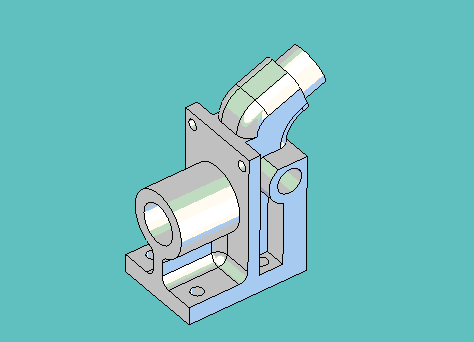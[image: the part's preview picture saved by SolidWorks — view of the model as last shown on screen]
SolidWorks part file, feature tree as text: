
SOLIDWORKS PART (.sldprt)
format: sldprt  version: not decoded by parser v0  size: 1,539,072 bytes
history: native  units: mm
features: sketch x19, boolean_combine x9, extrude x8, cut_extrude x8, fillet x3, material x1, revolve x1, chamfer x1, sweep x1 (+11 scaffold rows collapsed)
feature tree (62):
  scaffold x11  (default folders/planes/origin — collapsed)
  material  "Material <not specified>"
  sketch  "Sketch1"  dims[D1=4.7498mm D2=11.43mm D3=11.43mm D4=31.75mm]
  extrude  "Extrude1"  Depth=38.1mm
  sketch  "Sketch5"  dims[D1=5.7658mm D2=5.7658mm D3=14.1732mm]
  extrude  "Extrude7"  Depth=4.7752mm
  boolean_combine  "Combine4"
  sketch  "Sketch6"  dims[D2=7.366mm D1=20.6502mm]
  extrude  "Extrude8"  Depth=38.1mm
  boolean_combine  "Combine5"
  sketch  "Sketch7"  dims[D1=10.287mm]
  extrude  "Extrude10"  Depth=23.0632mm
  boolean_combine  "Combine6"
  sketch  "Sketch8"  dims[D1=6.604mm D2=4.7752mm]
  extrude  "Extrude11"  Depth=17.4498mm
  boolean_combine  "Combine7"
  sketch  "Sketch9"  dims[c1.D3=6.5278mm c1.D1=28.956mm c1.D2=4.7625mm c2.D1=27.1272mm]
  extrude  "Extrude12"  Depth=38.1mm
  boolean_combine  "Combine8"
  sketch  "Sketch11"  dims[c1.D1=0.381mm c1.D2=3.175mm c2.D1=3.175mm c2.D3=0.254mm c2.D4=7.62mm c2.D2=0.381mm]
  revolve  "Revolve2"  Angle=360deg
  boolean_combine  "Combine11"
  sketch  "Sketch12"  dims[c1.D1=3.175mm c1.D2=3.175mm c1.D3=3.175mm c1.D7=3.175mm c1.D4=9.525mm c1.D5=7.9248mm c1.D6=7.9248mm c2.D7=26.9748mm c2.D8=26.9748mm c2.D4=26.9875mm c2.D3=7.9248mm c2.D6=9.525mm c2.D5=7.9248mm c3.D8=7.9248mm c3.D9=9.525mm c4.D8=7.9248mm]
  extrude  "Extrude14"  Depth=12.7mm
  boolean_combine  "Combine12"
  chamfer  "Chamfer1"  Distance=0.889mm Angle=15deg
  sketch  "Sketch21"  dims[D1=3.175mm D2=15.875mm]
  cut_extrude  "Cut-Extrude6"  [1 undecoded]
  sketch  "Sketch24"  dims[c1.D2=2.032mm c1.D3=~2.38125mm c1.D4=~2.38125mm c1.D5=3.175mm c1.D1=4.7625mm c2.D3=3.175mm c2.D4=1.5875mm c2.D5=1.5875mm c2.D1=0.0mm]
  cut_extrude  "Cut-Extrude9"  [1 undecoded]
  fillet  "Fillet1"  Radius=2.38125mm
  sketch  "Sketch25"  dims[c1.D2=6.5278mm c1.D1=3.175mm c2.D2=22.225mm c2.D3=6.35mm c3.D2=1.778mm c3.D4=3.175mm c3.D5=7.9375mm c4.D4=31.75mm]
  cut_extrude  "Cut-Extrude10"  Depth=5.55625mm
  sketch  "Sketch26"  dims[D1=0.0mm]
  cut_extrude  "Cut-Extrude11"  Depth=5.55625mm
  sketch  "Sketch27"  dims[D3=2.7051mm D5=2.7051mm D1=34.925mm D2=8.89mm D4=8.89mm]
  cut_extrude  "Cut-Extrude12"  [1 undecoded]
  sketch  "Sketch29"  dims[D1=0.0mm]
  cut_extrude  "Cut-Extrude14"  Depth=6.35mm
  sketch  "Sketch30"
  sketch  "Sketch31"  dims[c1.D1=~20.20113mm c2.D1=68.0deg c2.D2=12.7mm c2.D3=6.35mm c2.D4=4.953mm c2.D5=4.953mm]
  sweep  "Sweep1"
  sketch  "Sketch32"  dims[c1.D1=9.525mm c1.D4=5.08mm c1.D3=6.35mm c2.D1=~7.666823mm c3.D1=54.0deg c3.D2=~15.09935mm c4.D2=42.0deg c4.D1=5.08mm c5.D2=5.08mm c5.D3=6.35mm c5.D1=~5.87502mm c6.D2=~5.87502mm]
  extrude  "Extrude15"  [1 undecoded]
  boolean_combine  "Combine13"
  boolean_combine  "Combine14"
  sketch  "Sketch33"  dims[D1=7.2644mm]
  cut_extrude  "Cut-Extrude15"  Depth=6.35mm
  sketch  "Sketch34"  dims[D2=10.414mm D3=3.175mm D4=3.175mm D1=0.0mm]
  cut_extrude  "Cut-Extrude16"  Depth=6.35mm
  fillet  "Fillet2"  Radius=3.175mm
  fillet  "Fillet3"  Radius=0.79375mm
decode coverage: 35 of 50 modeling features carry decoded parameters
note: ~ marks probable driven/reference dimensions
note: 4 parameter values undecoded
summary: no parameter record found for 4 features
note: suppression state not decoded; provenance and decode notes live in map.json
